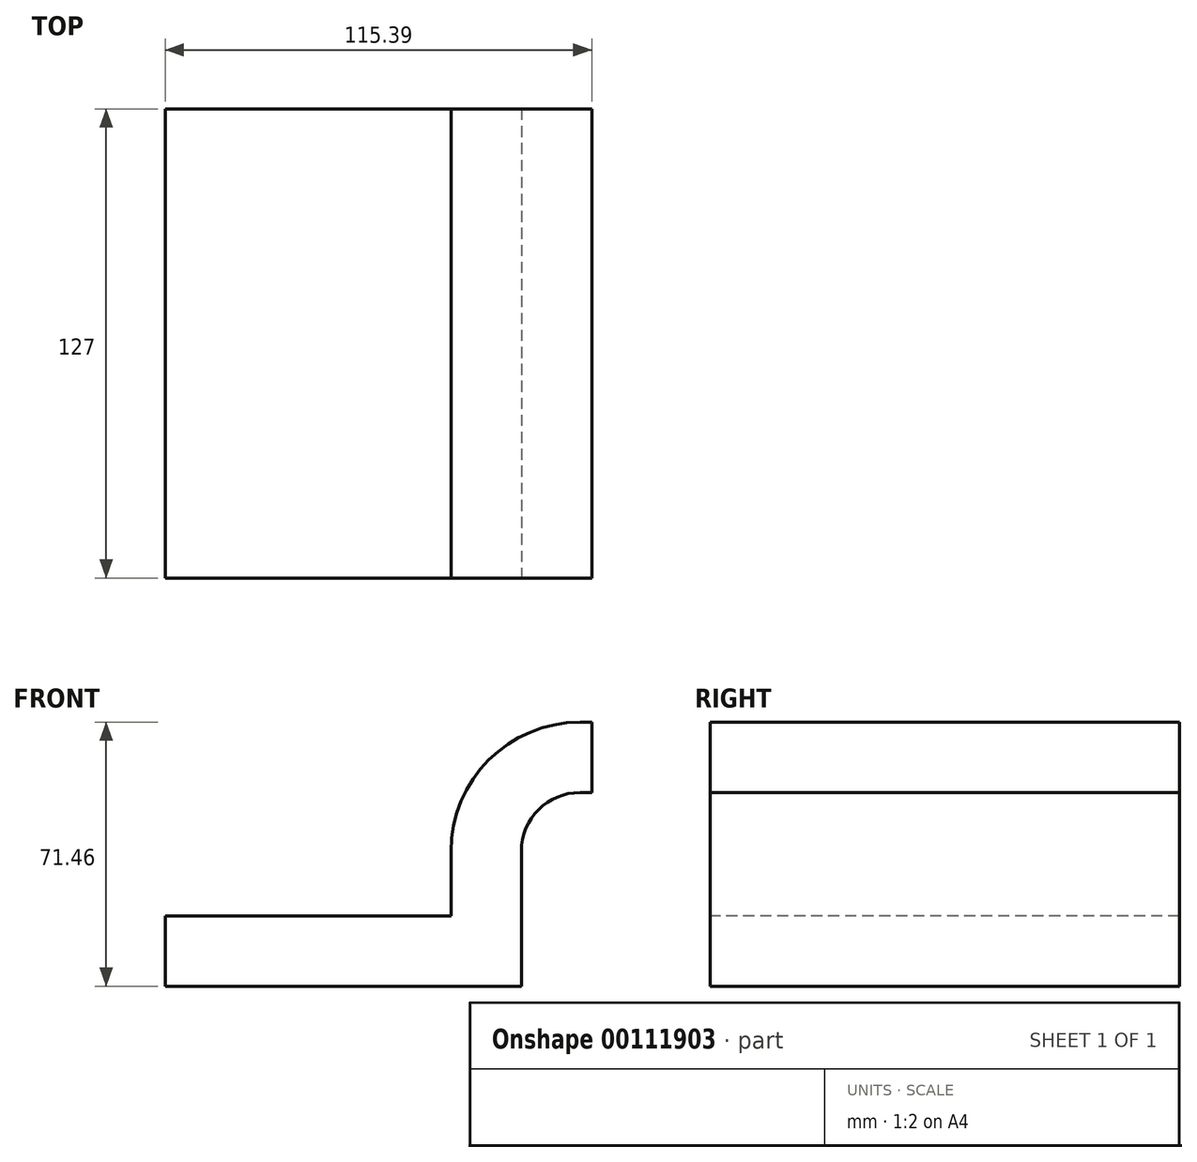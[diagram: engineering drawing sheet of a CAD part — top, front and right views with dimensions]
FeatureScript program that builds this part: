
annotation { "Feature Type Name" : "Feature", "Feature Type Description" : "" }
export const myFeature = defineFeature(function(context is Context, id is Id, definition is map)
    precondition{}
    {
        {
            var Q0;
            Q0=qCreatedBy(makeId("Front.planeOp"),FACE);
            var sketch = newSketch(context, id + "F0", { "sketchPlane" : qUnion([Q0])});
            skLineSegment(sketch, "E0.bottom", {"start": v(48.17, -9.52) * mm, "end": v(-48.17, -9.52) * mm});
            skLineSegment(sketch, "E0.top", {"start": v(48.17, 9.53) * mm, "end": v(-48.17, 9.53) * mm});
            skLineSegment(sketch, "E0.left", {"start": v(48.17, -9.52) * mm, "end": v(48.17, 9.53) * mm});
            skLineSegment(sketch, "E0.right", {"start": v(-48.17, -9.52) * mm, "end": v(-48.17, 9.53) * mm});
            skPoint(sketch, "E0.middle", {"position": v(0, 0) * mm});
            skLineSegment(sketch, "E1.bottom", {"start": v(67.22, 66.68) * mm, "end": v(118.02, 66.68) * mm});
            skLineSegment(sketch, "E1.top", {"start": v(67.22, 38.1) * mm, "end": v(118.02, 38.1) * mm});
            skLineSegment(sketch, "E1.left", {"start": v(67.22, 66.68) * mm, "end": v(67.22, 38.1) * mm});
            skLineSegment(sketch, "E1.right", {"start": v(118.02, 66.68) * mm, "end": v(118.02, 38.1) * mm});
            skLineSegment(sketch, "E2", {"start": v(48.17, 9.53) * mm, "end": v(48.17, 27) * mm});
            skArc(sketch, "E3", {"start": v(48.17, 27) * mm, "mid": v(52.82, 38.23) * mm, "end": v(64.05, 42.88) * mm});
            skLineSegment(sketch, "E4", {"start": v(64.05, 42.88) * mm, "end": v(92.62, 42.88) * mm});
            skArc(sketch, "E5.0", {"start": v(29.12, 27) * mm, "mid": v(39.35, 51.7) * mm, "end": v(64.05, 61.93) * mm});
            skLineSegment(sketch, "E6.0", {"start": v(29.12, 9.53) * mm, "end": v(29.12, 27) * mm});
            skLineSegment(sketch, "E7.0", {"start": v(64.05, 61.93) * mm, "end": v(92.62, 61.93) * mm});
            skLineSegment(sketch, "E8", {"start": v(92.62, 42.88) * mm, "end": v(92.62, 61.93) * mm});
            skLineSegment(sketch, "E9", {"start": v(92.62, 66.68) * mm, "end": v(92.62, 38.1) * mm});
            skFitSpline(sketch, "E10", {"points": [v(-48.17, 9.53) * mm, v(64.05, 61.93) * mm], "startDerivative": vector(98.32, 102.93) * mm, "endDerivative": vector(116.53, 0) * mm});
            skSolve(sketch);
        }
        {
            var Q0;
            Q0=makeQuery(id+"F0.imprint","IMPRINT",FACE,{"disambiguationData":[TD([[makeQuery(id+"F0.imprint","IMPRINT",EDGE,{"derivedFrom":sQuery(id+"F0.wireOp",EDGE,"E0.bottom")}),-1.0]])]});
            var Q1;
            {var subQ2=sQuery(id+"F0.wireOp",EDGE,"E2");Q1=makeQuery(id+"F0.imprint","IMPRINT",FACE,{"disambiguationData":[TD([[makeQuery(id+"F0.imprint","IMPRINT",EDGE,{"derivedFrom":subQ2}),1.0]])]});}
            extrude(context, id + "F1", {"entities" : qUnion([Q0, Q1]), "endBound" : BoundingType.SYMMETRIC, "oppositeDirection" : true, "depth" : 127 * mm});
        }
    });
